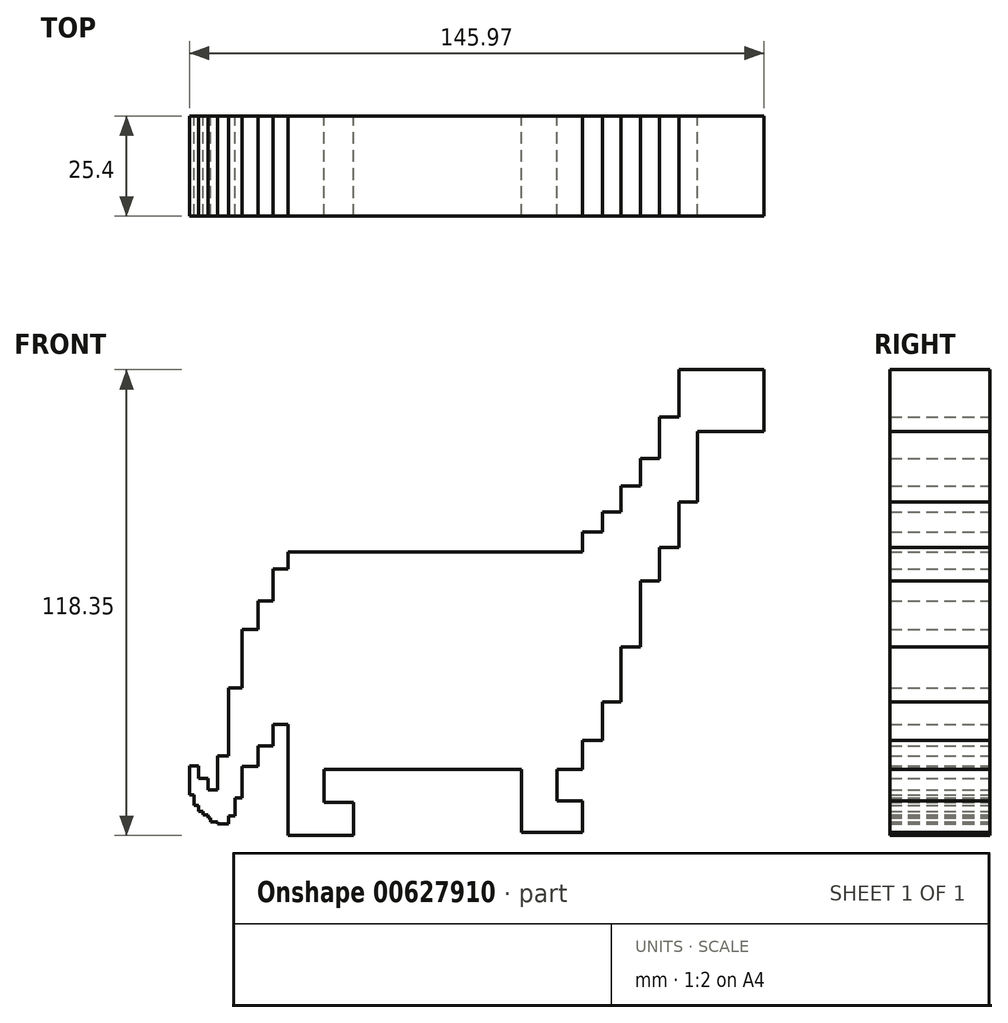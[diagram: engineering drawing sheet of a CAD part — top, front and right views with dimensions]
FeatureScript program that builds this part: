
annotation { "Feature Type Name" : "Feature", "Feature Type Description" : "" }
export const myFeature = defineFeature(function(context is Context, id is Id, definition is map)
    precondition{}
    {
        {
            var Q0;
            Q0=qCreatedBy(makeId("Front.planeOp"),FACE);
            var sketch = newSketch(context, id + "F0", { "sketchPlane" : qUnion([Q0])});
            skLineSegment(sketch, "E0.bottom", {"start": v(37.4, 27.61) * mm, "end": v(-37.4, 27.61) * mm});
            skLineSegment(sketch, "E0.top", {"start": v(37.4, -27.61) * mm, "end": v(-37.4, -27.61) * mm});
            skLineSegment(sketch, "E0.left", {"start": v(37.4, 27.61) * mm, "end": v(37.4, -27.61) * mm});
            skLineSegment(sketch, "E0.right", {"start": v(-37.4, 27.61) * mm, "end": v(-37.4, -27.61) * mm});
            skPoint(sketch, "E0.middle", {"position": v(0, 0) * mm});
            skLineSegment(sketch, "E1.bottom", {"start": v(-37.4, -27.61) * mm, "end": v(-28.31, -27.61) * mm});
            skLineSegment(sketch, "E1.top", {"start": v(-37.4, -44.39) * mm, "end": v(-28.31, -44.39) * mm});
            skLineSegment(sketch, "E1.left", {"start": v(-37.4, -27.61) * mm, "end": v(-37.4, -44.39) * mm});
            skLineSegment(sketch, "E1.right", {"start": v(-28.31, -27.61) * mm, "end": v(-28.31, -44.39) * mm});
            skPoint(sketch, "E2.oppositeSnap0", {"position": v(-28.31, -36) * mm});
            skLineSegment(sketch, "E2.bottom", {"start": v(-28.31, -44.39) * mm, "end": v(-20.8, -44.39) * mm});
            skLineSegment(sketch, "E2.top", {"start": v(-28.31, -36) * mm, "end": v(-20.8, -36) * mm});
            skLineSegment(sketch, "E2.left", {"start": v(-28.31, -44.39) * mm, "end": v(-28.31, -36) * mm});
            skLineSegment(sketch, "E2.right", {"start": v(-20.8, -44.39) * mm, "end": v(-20.8, -36) * mm});
            skLineSegment(sketch, "E3.bottom", {"start": v(21.85, -27.61) * mm, "end": v(30.94, -27.61) * mm});
            skLineSegment(sketch, "E3.top", {"start": v(21.85, -43.56) * mm, "end": v(30.94, -43.56) * mm});
            skLineSegment(sketch, "E3.left", {"start": v(21.85, -27.61) * mm, "end": v(21.85, -43.56) * mm});
            skLineSegment(sketch, "E3.right", {"start": v(30.94, -27.61) * mm, "end": v(30.94, -43.56) * mm});
            skLineSegment(sketch, "E4.bottom", {"start": v(30.94, -35.59) * mm, "end": v(37.4, -35.59) * mm});
            skLineSegment(sketch, "E4.top", {"start": v(30.94, -43.56) * mm, "end": v(37.4, -43.56) * mm});
            skLineSegment(sketch, "E4.left", {"start": v(30.94, -35.59) * mm, "end": v(30.94, -43.56) * mm});
            skLineSegment(sketch, "E4.right", {"start": v(37.4, -35.59) * mm, "end": v(37.4, -43.56) * mm});
            skPoint(sketch, "E5.oppositeSnap0", {"position": v(21.85, -35.59) * mm});
            skPoint(sketch, "E5.oppositeSnap1", {"position": v(26.4, -27.61) * mm});
            skLineSegment(sketch, "E5.bottom", {"start": v(21.85, -35.59) * mm, "end": v(26.4, -35.59) * mm});
            skLineSegment(sketch, "E5.top", {"start": v(21.85, -35.59) * mm, "end": v(26.4, -35.59) * mm});
            skLineSegment(sketch, "E5.left", {"start": v(21.85, -35.59) * mm, "end": v(21.85, -35.59) * mm});
            skLineSegment(sketch, "E5.right", {"start": v(26.4, -35.59) * mm, "end": v(26.4, -35.59) * mm});
            skLineSegment(sketch, "E6.bottom", {"start": v(-37.4, 23.29) * mm, "end": v(-41.2, 23.29) * mm});
            skLineSegment(sketch, "E6.top", {"start": v(-37.4, -16.2) * mm, "end": v(-41.2, -16.2) * mm});
            skLineSegment(sketch, "E6.left", {"start": v(-37.4, 23.29) * mm, "end": v(-37.4, -16.2) * mm});
            skLineSegment(sketch, "E6.right", {"start": v(-41.2, 23.29) * mm, "end": v(-41.2, -16.2) * mm});
            skLineSegment(sketch, "E7.bottom", {"start": v(-41.2, 15.12) * mm, "end": v(-45.07, 15.12) * mm});
            skLineSegment(sketch, "E7.top", {"start": v(-41.2, -21.71) * mm, "end": v(-45.07, -21.71) * mm});
            skLineSegment(sketch, "E7.left", {"start": v(-41.2, 15.12) * mm, "end": v(-41.2, -21.71) * mm});
            skLineSegment(sketch, "E7.right", {"start": v(-45.07, 15.12) * mm, "end": v(-45.07, -21.71) * mm});
            skLineSegment(sketch, "E8.bottom", {"start": v(-45.07, 7.97) * mm, "end": v(-49.12, 7.97) * mm});
            skLineSegment(sketch, "E8.top", {"start": v(-45.07, -26.9) * mm, "end": v(-49.12, -26.9) * mm});
            skLineSegment(sketch, "E8.left", {"start": v(-45.07, 7.97) * mm, "end": v(-45.07, -26.9) * mm});
            skLineSegment(sketch, "E8.right", {"start": v(-49.12, 7.97) * mm, "end": v(-49.12, -26.9) * mm});
            skLineSegment(sketch, "E9.bottom", {"start": v(-49.12, -6.9) * mm, "end": v(-52.54, -6.9) * mm});
            skLineSegment(sketch, "E9.top", {"start": v(-49.12, -34.87) * mm, "end": v(-52.54, -34.87) * mm});
            skLineSegment(sketch, "E9.left", {"start": v(-49.12, -6.9) * mm, "end": v(-49.12, -34.87) * mm});
            skLineSegment(sketch, "E9.right", {"start": v(-52.54, -6.9) * mm, "end": v(-52.54, -34.87) * mm});
            skLineSegment(sketch, "E10.bottom", {"start": v(-52.54, -24.22) * mm, "end": v(-55.3, -24.22) * mm});
            skLineSegment(sketch, "E10.top", {"start": v(-52.54, -41.47) * mm, "end": v(-55.3, -41.47) * mm});
            skLineSegment(sketch, "E10.left", {"start": v(-52.54, -24.22) * mm, "end": v(-52.54, -41.47) * mm});
            skLineSegment(sketch, "E10.right", {"start": v(-55.3, -24.22) * mm, "end": v(-55.3, -41.47) * mm});
            skLineSegment(sketch, "E11.bottom", {"start": v(-55.3, -32.84) * mm, "end": v(-57.77, -32.84) * mm});
            skLineSegment(sketch, "E11.top", {"start": v(-55.3, -39.88) * mm, "end": v(-57.77, -39.88) * mm});
            skLineSegment(sketch, "E11.left", {"start": v(-55.3, -32.84) * mm, "end": v(-55.3, -39.88) * mm});
            skLineSegment(sketch, "E11.right", {"start": v(-57.77, -32.84) * mm, "end": v(-57.77, -39.88) * mm});
            skLineSegment(sketch, "E12.bottom", {"start": v(-57.77, -38.3) * mm, "end": v(-60.09, -38.3) * mm});
            skLineSegment(sketch, "E12.top", {"start": v(-57.77, -29.87) * mm, "end": v(-60.09, -29.87) * mm});
            skLineSegment(sketch, "E12.left", {"start": v(-57.77, -38.3) * mm, "end": v(-57.77, -29.87) * mm});
            skLineSegment(sketch, "E12.right", {"start": v(-60.09, -38.3) * mm, "end": v(-60.09, -29.87) * mm});
            skLineSegment(sketch, "E13.bottom", {"start": v(-60.09, -34.08) * mm, "end": v(-62.44, -34.08) * mm});
            skLineSegment(sketch, "E13.top", {"start": v(-60.09, -26.68) * mm, "end": v(-62.44, -26.68) * mm});
            skLineSegment(sketch, "E13.left", {"start": v(-60.09, -34.08) * mm, "end": v(-60.09, -26.68) * mm});
            skLineSegment(sketch, "E13.right", {"start": v(-62.44, -34.08) * mm, "end": v(-62.44, -26.68) * mm});
            skPoint(sketch, "E14.oppositeSnap0", {"position": v(-50.83, -34.87) * mm});
            skLineSegment(sketch, "E14.bottom", {"start": v(-52.54, -34.87) * mm, "end": v(-50.83, -34.87) * mm});
            skLineSegment(sketch, "E14.top", {"start": v(-52.54, -39.46) * mm, "end": v(-50.83, -39.46) * mm});
            skLineSegment(sketch, "E14.left", {"start": v(-52.54, -34.87) * mm, "end": v(-52.54, -39.46) * mm});
            skLineSegment(sketch, "E14.right", {"start": v(-50.83, -34.87) * mm, "end": v(-50.83, -39.46) * mm});
            skPoint(sketch, "E15.oppositeSnap0", {"position": v(-61.26, -34.08) * mm});
            skLineSegment(sketch, "E15.bottom", {"start": v(-60.09, -34.08) * mm, "end": v(-61.26, -34.08) * mm});
            skLineSegment(sketch, "E15.top", {"start": v(-60.09, -36.71) * mm, "end": v(-61.26, -36.71) * mm});
            skLineSegment(sketch, "E15.left", {"start": v(-60.09, -34.08) * mm, "end": v(-60.09, -36.71) * mm});
            skLineSegment(sketch, "E15.right", {"start": v(-61.26, -34.08) * mm, "end": v(-61.26, -36.71) * mm});
            skPoint(sketch, "E16.oppositeSnap0", {"position": v(-58.93, -38.3) * mm});
            skLineSegment(sketch, "E16.bottom", {"start": v(-57.77, -38.3) * mm, "end": v(-58.93, -38.3) * mm});
            skLineSegment(sketch, "E16.top", {"start": v(-57.77, -39.2) * mm, "end": v(-58.93, -39.2) * mm});
            skLineSegment(sketch, "E16.left", {"start": v(-57.77, -38.3) * mm, "end": v(-57.77, -39.2) * mm});
            skLineSegment(sketch, "E16.right", {"start": v(-58.93, -38.3) * mm, "end": v(-58.93, -39.2) * mm});
            skLineSegment(sketch, "E17.bottom", {"start": v(-55.3, -39.88) * mm, "end": v(-57.07, -39.88) * mm});
            skLineSegment(sketch, "E17.top", {"start": v(-55.3, -40.94) * mm, "end": v(-57.07, -40.94) * mm});
            skLineSegment(sketch, "E17.left", {"start": v(-55.3, -39.88) * mm, "end": v(-55.3, -40.94) * mm});
            skLineSegment(sketch, "E17.right", {"start": v(-57.07, -39.88) * mm, "end": v(-57.07, -40.94) * mm});
            skLineSegment(sketch, "E18.bottom", {"start": v(37.4, -20.25) * mm, "end": v(42.42, -20.25) * mm});
            skLineSegment(sketch, "E18.top", {"start": v(37.4, 32.75) * mm, "end": v(42.42, 32.75) * mm});
            skLineSegment(sketch, "E18.left", {"start": v(37.4, -20.25) * mm, "end": v(37.4, 32.75) * mm});
            skLineSegment(sketch, "E18.right", {"start": v(42.42, -20.25) * mm, "end": v(42.42, 32.75) * mm});
            skLineSegment(sketch, "E19.bottom", {"start": v(42.42, -10.52) * mm, "end": v(47.24, -10.52) * mm});
            skLineSegment(sketch, "E19.top", {"start": v(42.42, 37.8) * mm, "end": v(47.24, 37.8) * mm});
            skLineSegment(sketch, "E19.left", {"start": v(42.42, -10.52) * mm, "end": v(42.42, 37.8) * mm});
            skLineSegment(sketch, "E19.right", {"start": v(47.24, -10.52) * mm, "end": v(47.24, 37.8) * mm});
            skLineSegment(sketch, "E20.bottom", {"start": v(47.24, 3.53) * mm, "end": v(52.1, 3.53) * mm});
            skLineSegment(sketch, "E20.top", {"start": v(47.24, 44.38) * mm, "end": v(52.1, 44.38) * mm});
            skLineSegment(sketch, "E20.left", {"start": v(47.24, 3.53) * mm, "end": v(47.24, 44.38) * mm});
            skLineSegment(sketch, "E20.right", {"start": v(52.1, 3.53) * mm, "end": v(52.1, 44.38) * mm});
            skLineSegment(sketch, "E21.bottom", {"start": v(52.1, 20.26) * mm, "end": v(57.02, 20.26) * mm});
            skLineSegment(sketch, "E21.top", {"start": v(52.1, 51.38) * mm, "end": v(57.02, 51.38) * mm});
            skLineSegment(sketch, "E21.left", {"start": v(52.1, 20.26) * mm, "end": v(52.1, 51.38) * mm});
            skLineSegment(sketch, "E21.right", {"start": v(57.02, 20.26) * mm, "end": v(57.02, 51.38) * mm});
            skLineSegment(sketch, "E22.bottom", {"start": v(57.02, 35.82) * mm, "end": v(61.9, 35.82) * mm});
            skLineSegment(sketch, "E22.top", {"start": v(57.02, 61.95) * mm, "end": v(61.9, 61.95) * mm});
            skLineSegment(sketch, "E22.left", {"start": v(57.02, 35.82) * mm, "end": v(57.02, 61.95) * mm});
            skLineSegment(sketch, "E22.right", {"start": v(61.9, 35.82) * mm, "end": v(61.9, 61.95) * mm});
            skLineSegment(sketch, "E23.bottom", {"start": v(57.02, 28.7) * mm, "end": v(61.9, 28.7) * mm});
            skLineSegment(sketch, "E23.left", {"start": v(57.02, 28.7) * mm, "end": v(57.02, 35.82) * mm});
            skLineSegment(sketch, "E23.right", {"start": v(61.9, 28.7) * mm, "end": v(61.9, 35.82) * mm});
            skLineSegment(sketch, "E24.bottom", {"start": v(61.9, 40.3) * mm, "end": v(66.63, 40.3) * mm});
            skLineSegment(sketch, "E24.top", {"start": v(61.9, 73.96) * mm, "end": v(66.63, 73.96) * mm});
            skLineSegment(sketch, "E24.left", {"start": v(61.9, 40.3) * mm, "end": v(61.9, 73.96) * mm});
            skLineSegment(sketch, "E24.right", {"start": v(66.63, 40.3) * mm, "end": v(66.63, 73.96) * mm});
            skLineSegment(sketch, "E25.bottom", {"start": v(66.63, 73.96) * mm, "end": v(83.53, 73.96) * mm});
            skLineSegment(sketch, "E25.top", {"start": v(66.63, 58.23) * mm, "end": v(83.53, 58.23) * mm});
            skLineSegment(sketch, "E25.left", {"start": v(66.63, 73.96) * mm, "end": v(66.63, 58.23) * mm});
            skLineSegment(sketch, "E25.right", {"start": v(83.53, 73.96) * mm, "end": v(83.53, 58.23) * mm});
            skLineSegment(sketch, "E26", {"start": v(-24.55, -44.39) * mm, "end": v(-24.55, -40.73) * mm});
            skPoint(sketch, "E26.endSnap0", {"position": v(-24.55, -44.39) * mm});
            skLineSegment(sketch, "E27", {"start": v(-20.8, -40.73) * mm, "end": v(-24.55, -40.73) * mm});
            skLineSegment(sketch, "E28", {"start": v(34.17, -43.56) * mm, "end": v(34.17, -40.17) * mm});
            skLineSegment(sketch, "E29", {"start": v(37.4, -40.17) * mm, "end": v(34.17, -40.17) * mm});
            skSolve(sketch);
        }
        {
            var Q0;
            Q0 = qSketchRegion(id + "F0", true);
            extrude(context, id + "F1", {"entities" : qUnion([Q0]), "depth" : 25.4 * mm, "offsetDistance" : 25.4 * mm});
        }
    });
